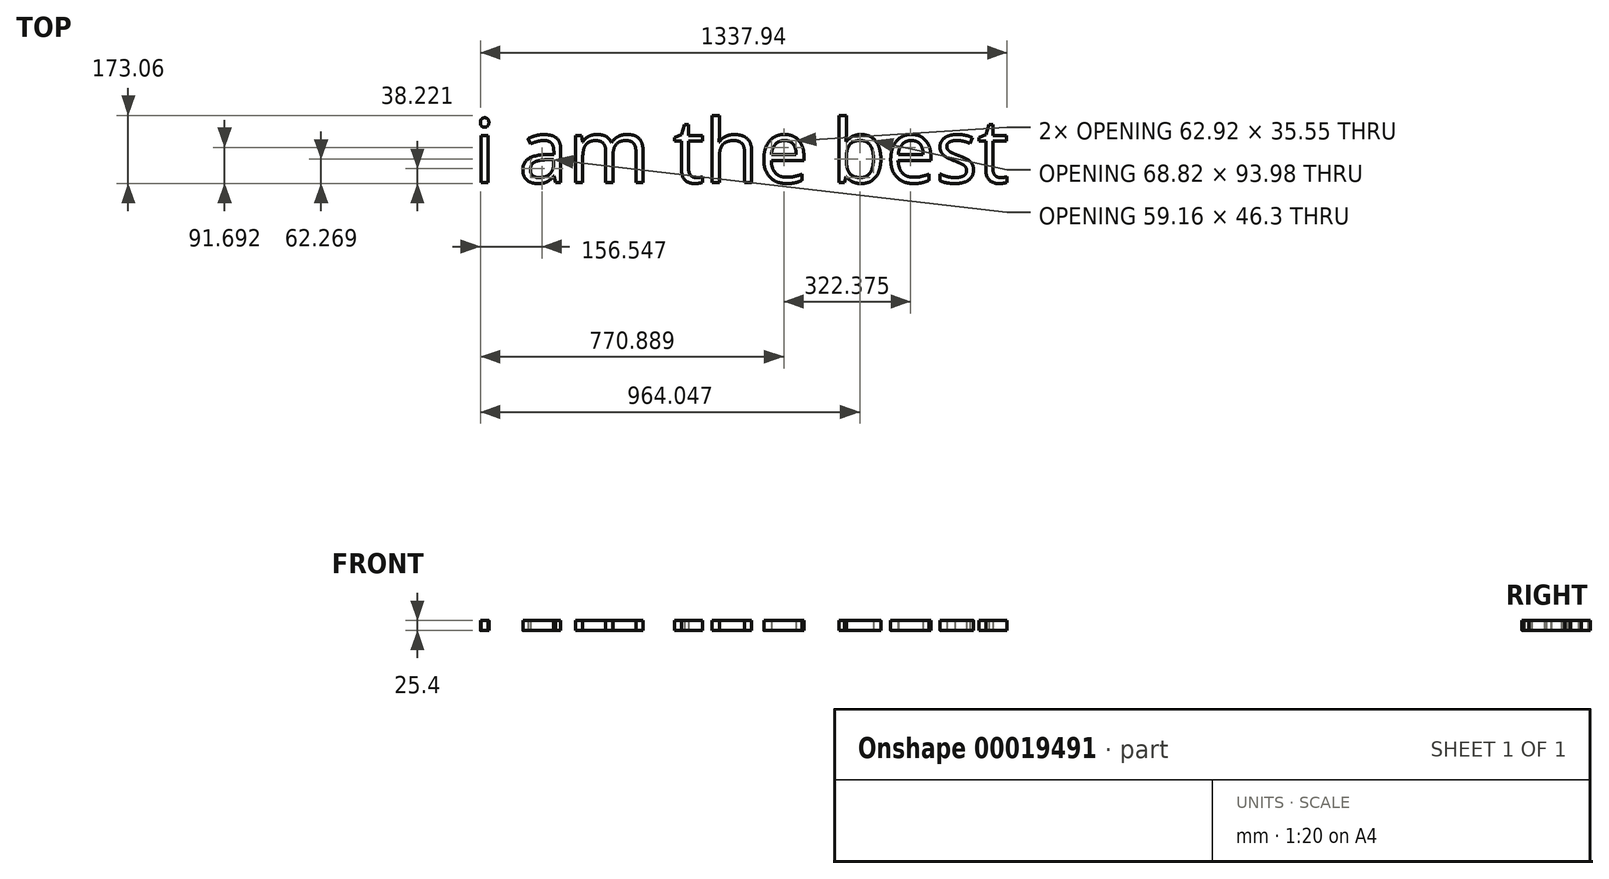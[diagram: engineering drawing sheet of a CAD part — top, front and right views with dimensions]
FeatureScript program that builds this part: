
annotation { "Feature Type Name" : "Feature", "Feature Type Description" : "" }
export const myFeature = defineFeature(function(context is Context, id is Id, definition is map)
    precondition{}
    {
        {
            var Q0;
            Q0=qCreatedBy(makeId("Top.planeOp"),FACE);
            var sketch = newSketch(context, id + "F0", { "sketchPlane" : qUnion([Q0])});
            skText(sketch, "E0", { "text": "i am the best", "fontName": "OpenSans-Regular.ttf"});
            const initialGuessF0  = {"E0": [-0.13387, -0.09628, 1, 0, 0.16189]};
            skSetInitialGuess(sketch, initialGuessF0);
            skSolve(sketch);
        }
        {
            var Q0;
            Q0 = qSketchRegion(id + "F0", true);
            extrude(context, id + "F1", {"entities" : qUnion([Q0]), "depth" : 25.4 * mm});
        }
    });
